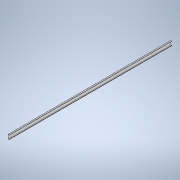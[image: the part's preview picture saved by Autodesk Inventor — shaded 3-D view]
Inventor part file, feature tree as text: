
AUTODESK INVENTOR PART (.ipt)
format: ipt  version: 2020 (Build 240168000, 168)  size: 111,616 bytes
history: native  units: mm
features: extrude x1, sketch x1
ambient origin geometry x8: Origin, YZ Plane, XZ Plane, XY Plane, X Axis, Y Axis, Z Axis, Center Point
bodies: Solid1 (feature_tree)
feature tree (2):
  extrude  "Extrusion1"  Depth=150.0mm
  sketch  "Sketch1"  dims[d0=43.0mm d1=150.0mm d2=15.0mm d3=15.0mm d4=2.5mm d5=6000.0mm d6=0.0mm]
